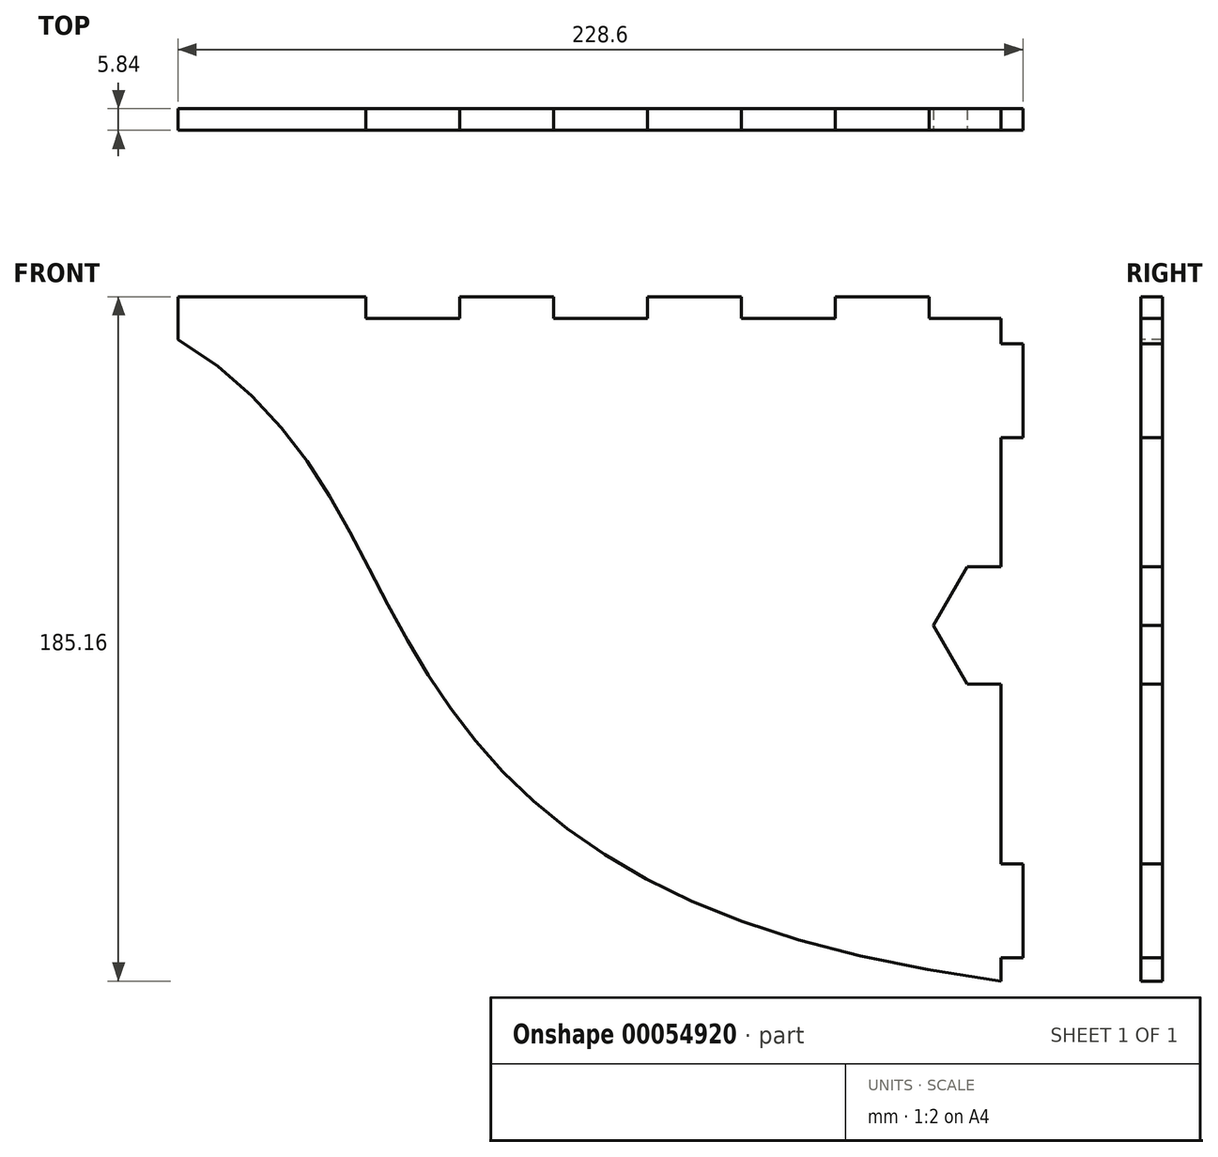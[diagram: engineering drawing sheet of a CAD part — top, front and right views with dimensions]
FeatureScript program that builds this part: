
annotation { "Feature Type Name" : "Feature", "Feature Type Description" : "" }
export const myFeature = defineFeature(function(context is Context, id is Id, definition is map)
    precondition{}
    {
        {
            var Q0;
            Q0=qCreatedBy(makeId("Front.planeOp"),FACE);
            var sketch = newSketch(context, id + "F0", { "sketchPlane" : qUnion([Q0])});
            skLineSegment(sketch, "E0.bottom", {"start": v(-113.95, 205.98) * mm, "end": v(165.45, 205.98) * mm});
            skLineSegment(sketch, "E0.top", {"start": v(-113.95, -124.22) * mm, "end": v(165.45, -124.22) * mm});
            skLineSegment(sketch, "E0.left", {"start": v(-113.95, 205.98) * mm, "end": v(-113.95, -124.22) * mm});
            skLineSegment(sketch, "E0.right", {"start": v(165.45, 205.98) * mm, "end": v(165.45, -124.22) * mm});
            skSolve(sketch);
        }
        {
            var Q0;
            Q0=makeQuery(id+"F0.imprint","IMPRINT",FACE,{"disambiguationData":[TD([[makeQuery(id+"F0.imprint","IMPRINT",EDGE,{"derivedFrom":sQuery(id+"F0.wireOp",EDGE,"E0.bottom")}),-1.0]])]});
            extrude(context, id + "F1", {"entities" : qUnion([Q0]), "depth" : 5.84 * mm});
        }
        {
            var Q0;
            Q0=makeQuery(id+"F1.opExtrude","CAP_FACE",FACE,{"disambiguationData":[OSD([sQuery(id+"F0.wireOp",EDGE,"E0.bottom"),sQuery(id+"F0.wireOp",EDGE,"E0.top"),sQuery(id+"F0.wireOp",EDGE,"E0.left"),sQuery(id+"F0.wireOp",EDGE,"E0.right")])],"isStart":false});
            var sketch = newSketch(context, id + "F2", { "sketchPlane" : qUnion([Q0])});
            skLineSegment(sketch, "E1", {"start": v(165.45, -118.38) * mm, "end": v(140.05, -118.38) * mm});
            skLineSegment(sketch, "E2", {"start": v(140.05, -118.38) * mm, "end": v(140.05, -124.22) * mm});
            skLineSegment(sketch, "E3", {"start": v(140.05, -124.22) * mm, "end": v(114.65, -124.22) * mm});
            skLineSegment(sketch, "E4", {"start": v(114.65, -124.22) * mm, "end": v(114.65, -118.38) * mm});
            skLineSegment(sketch, "E5", {"start": v(114.65, -118.38) * mm, "end": v(89.25, -118.38) * mm});
            skLineSegment(sketch, "E6", {"start": v(89.25, -118.38) * mm, "end": v(89.25, -124.22) * mm});
            skLineSegment(sketch, "E7", {"start": v(89.25, -124.22) * mm, "end": v(63.85, -124.22) * mm});
            skLineSegment(sketch, "E8", {"start": v(63.85, -124.22) * mm, "end": v(63.85, -118.38) * mm});
            skLineSegment(sketch, "E9", {"start": v(63.85, -118.38) * mm, "end": v(38.45, -118.38) * mm});
            skLineSegment(sketch, "E10", {"start": v(38.45, -118.38) * mm, "end": v(38.45, -124.22) * mm});
            skLineSegment(sketch, "E11", {"start": v(38.45, -124.22) * mm, "end": v(13.05, -124.22) * mm});
            skLineSegment(sketch, "E12", {"start": v(13.05, -124.22) * mm, "end": v(13.05, -118.38) * mm});
            skLineSegment(sketch, "E13", {"start": v(13.05, -118.38) * mm, "end": v(-12.35, -118.38) * mm});
            skLineSegment(sketch, "E14", {"start": v(-12.35, -118.38) * mm, "end": v(-12.35, -124.22) * mm});
            skLineSegment(sketch, "E15", {"start": v(-12.35, -124.22) * mm, "end": v(-37.75, -124.22) * mm});
            skLineSegment(sketch, "E16", {"start": v(-37.75, -124.22) * mm, "end": v(-37.75, -118.38) * mm});
            skLineSegment(sketch, "E17", {"start": v(-37.75, -118.38) * mm, "end": v(-113.95, -118.38) * mm});
            skLineSegment(sketch, "E18", {"start": v(-113.95, -118.38) * mm, "end": v(-113.95, -124.22) * mm});
            skLineSegment(sketch, "E19", {"start": v(-113.95, -124.22) * mm, "end": v(-37.75, -124.22) * mm});
            skLineSegment(sketch, "E20.bottom", {"start": v(165.45, -98.82) * mm, "end": v(159.6, -98.82) * mm});
            skLineSegment(sketch, "E20.top", {"start": v(165.45, -73.42) * mm, "end": v(159.6, -73.42) * mm});
            skLineSegment(sketch, "E20.left", {"start": v(165.45, -98.82) * mm, "end": v(165.45, -73.42) * mm});
            skLineSegment(sketch, "E20.right", {"start": v(159.6, -98.82) * mm, "end": v(159.6, -73.42) * mm});
            skLineSegment(sketch, "E21.bottom", {"start": v(165.45, -48.02) * mm, "end": v(159.6, -48.02) * mm});
            skLineSegment(sketch, "E21.top", {"start": v(165.45, -9.92) * mm, "end": v(159.6, -9.92) * mm});
            skLineSegment(sketch, "E21.left", {"start": v(165.45, -48.02) * mm, "end": v(165.45, -9.92) * mm});
            skLineSegment(sketch, "E21.right", {"start": v(159.6, -48.02) * mm, "end": v(159.6, -9.92) * mm});
            skLineSegment(sketch, "E22.bottom", {"start": v(-113.95, -98.82) * mm, "end": v(-108.1, -98.82) * mm});
            skLineSegment(sketch, "E22.top", {"start": v(-113.95, -73.42) * mm, "end": v(-108.1, -73.42) * mm});
            skLineSegment(sketch, "E22.left", {"start": v(-113.95, -98.82) * mm, "end": v(-113.95, -73.42) * mm});
            skLineSegment(sketch, "E22.right", {"start": v(-108.1, -98.82) * mm, "end": v(-108.1, -73.42) * mm});
            skLineSegment(sketch, "E23.bottom", {"start": v(-113.95, -48.02) * mm, "end": v(-108.1, -48.02) * mm});
            skLineSegment(sketch, "E23.top", {"start": v(-113.95, -22.62) * mm, "end": v(-108.1, -22.62) * mm});
            skLineSegment(sketch, "E23.left", {"start": v(-113.95, -48.02) * mm, "end": v(-113.95, -22.62) * mm});
            skLineSegment(sketch, "E23.right", {"start": v(-108.1, -48.02) * mm, "end": v(-108.1, -22.62) * mm});
            skLineSegment(sketch, "E24.bottom", {"start": v(-113.95, 2.78) * mm, "end": v(-108.1, 2.78) * mm});
            skLineSegment(sketch, "E24.top", {"start": v(-113.95, 28.18) * mm, "end": v(-108.1, 28.18) * mm});
            skLineSegment(sketch, "E24.left", {"start": v(-113.95, 2.78) * mm, "end": v(-113.95, 28.18) * mm});
            skLineSegment(sketch, "E24.right", {"start": v(-108.1, 2.78) * mm, "end": v(-108.1, 28.18) * mm});
            skLineSegment(sketch, "E25.bottom", {"start": v(-113.95, 104.38) * mm, "end": v(-108.1, 104.38) * mm});
            skLineSegment(sketch, "E25.top", {"start": v(-113.95, 129.78) * mm, "end": v(-108.1, 129.78) * mm});
            skLineSegment(sketch, "E25.left", {"start": v(-113.95, 104.38) * mm, "end": v(-113.95, 129.78) * mm});
            skLineSegment(sketch, "E25.right", {"start": v(-108.1, 104.38) * mm, "end": v(-108.1, 129.78) * mm});
            skLineSegment(sketch, "E26.bottom", {"start": v(-113.95, 53.58) * mm, "end": v(-108.1, 53.58) * mm});
            skLineSegment(sketch, "E26.top", {"start": v(-113.95, 78.98) * mm, "end": v(-108.1, 78.98) * mm});
            skLineSegment(sketch, "E26.left", {"start": v(-113.95, 53.58) * mm, "end": v(-113.95, 78.98) * mm});
            skLineSegment(sketch, "E26.right", {"start": v(-108.1, 53.58) * mm, "end": v(-108.1, 78.98) * mm});
            skLineSegment(sketch, "E27.bottom", {"start": v(-113.95, 155.18) * mm, "end": v(-108.1, 155.18) * mm});
            skLineSegment(sketch, "E27.top", {"start": v(-113.95, 180.58) * mm, "end": v(-108.1, 180.58) * mm});
            skLineSegment(sketch, "E27.left", {"start": v(-113.95, 155.18) * mm, "end": v(-113.95, 180.58) * mm});
            skLineSegment(sketch, "E27.right", {"start": v(-108.1, 155.18) * mm, "end": v(-108.1, 180.58) * mm});
            skSolve(sketch);
        }
        {
            var Q0;
            {var subQ0=sQuery(id+"F2.wireOp",EDGE,"E1");Q0=makeQuery(id+"F2.imprint","IMPRINT",FACE,{"disambiguationData":[TD([[makeQuery(id+"F2.imprint","IMPRINT",EDGE,{"derivedFrom":subQ0}),1.0]])]});}
            var Q1;
            {var subQ0=sQuery(id+"F2.wireOp",EDGE,"E4");Q1=makeQuery(id+"F2.imprint","IMPRINT",FACE,{"disambiguationData":[TD([[makeQuery(id+"F2.imprint","IMPRINT",EDGE,{"derivedFrom":subQ0}),1.0]])]});}
            var Q2;
            {var subQ0=sQuery(id+"F2.wireOp",EDGE,"E8");Q2=makeQuery(id+"F2.imprint","IMPRINT",FACE,{"disambiguationData":[TD([[makeQuery(id+"F2.imprint","IMPRINT",EDGE,{"derivedFrom":subQ0}),1.0]])]});}
            var Q3;
            {var subQ0=sQuery(id+"F2.wireOp",EDGE,"E12");Q3=makeQuery(id+"F2.imprint","IMPRINT",FACE,{"disambiguationData":[TD([[makeQuery(id+"F2.imprint","IMPRINT",EDGE,{"derivedFrom":subQ0}),1.0]])]});}
            var Q4;
            Q4=makeQuery(id+"F2.imprint","IMPRINT",FACE,{"disambiguationData":[TD([[makeQuery(id+"F2.imprint","IMPRINT",EDGE,{"derivedFrom":sQuery(id+"F2.wireOp",EDGE,"E16")}),1.0]])]});
            var Q5;
            Q5=makeQuery(id+"F2.imprint","IMPRINT",FACE,{"disambiguationData":[TD([[makeQuery(id+"F2.imprint","IMPRINT",EDGE,{"derivedFrom":sQuery(id+"F2.wireOp",EDGE,"E20.bottom")}),-1.0]])]});
            var Q6;
            Q6=makeQuery(id+"F2.imprint","IMPRINT",FACE,{"disambiguationData":[TD([[makeQuery(id+"F2.imprint","IMPRINT",EDGE,{"derivedFrom":sQuery(id+"F2.wireOp",EDGE,"E21.bottom")}),-1.0]])]});
            var Q7;
            Q7=makeQuery(id+"F2.imprint","IMPRINT",FACE,{"disambiguationData":[TD([[makeQuery(id+"F2.imprint","IMPRINT",EDGE,{"derivedFrom":sQuery(id+"F2.wireOp",EDGE,"E22.bottom")}),1.0]])]});
            var Q8;
            Q8=makeQuery(id+"F2.imprint","IMPRINT",FACE,{"disambiguationData":[TD([[makeQuery(id+"F2.imprint","IMPRINT",EDGE,{"derivedFrom":sQuery(id+"F2.wireOp",EDGE,"E23.bottom")}),1.0]])]});
            var Q9;
            Q9=makeQuery(id+"F2.imprint","IMPRINT",FACE,{"disambiguationData":[TD([[makeQuery(id+"F2.imprint","IMPRINT",EDGE,{"derivedFrom":sQuery(id+"F2.wireOp",EDGE,"E24.bottom")}),1.0]])]});
            var Q10;
            Q10=makeQuery(id+"F2.imprint","IMPRINT",FACE,{"disambiguationData":[TD([[makeQuery(id+"F2.imprint","IMPRINT",EDGE,{"derivedFrom":sQuery(id+"F2.wireOp",EDGE,"E26.bottom")}),1.0]])]});
            var Q11;
            Q11=makeQuery(id+"F2.imprint","IMPRINT",FACE,{"disambiguationData":[TD([[makeQuery(id+"F2.imprint","IMPRINT",EDGE,{"derivedFrom":sQuery(id+"F2.wireOp",EDGE,"E27.bottom")}),1.0]])]});
            var Q12;
            Q12=makeQuery(id+"F2.imprint","IMPRINT",FACE,{"disambiguationData":[TD([[makeQuery(id+"F2.imprint","IMPRINT",EDGE,{"derivedFrom":sQuery(id+"F2.wireOp",EDGE,"E25.bottom")}),1.0]])]});
            var Q13;
            Q13=makeQuery(id+"F1.opExtrude","CAP_FACE",FACE,{"disambiguationData":[OSD([sQuery(id+"F0.wireOp",EDGE,"E0.bottom"),sQuery(id+"F0.wireOp",EDGE,"E0.top"),sQuery(id+"F0.wireOp",EDGE,"E0.left"),sQuery(id+"F0.wireOp",EDGE,"E0.right")])],"isStart":true});
            extrude(context, id + "F3", {"entities" : qUnion([Q0, Q1, Q2, Q3, Q4, Q5, Q6, Q7, Q8, Q9, Q10, Q11, Q12]), "operationType" : NewBodyOperationType.REMOVE, "endBound" : BoundingType.UP_TO_SURFACE, "oppositeDirection" : true, "endBoundEntityFace" : qUnion([Q13]), "depth" : 25.4 * mm});
        }
        {
            var Q0;
            Q0=makeQuery(id+"F1.opExtrude","CAP_FACE",FACE,{"disambiguationData":[OSD([sQuery(id+"F0.wireOp",EDGE,"E0.bottom"),sQuery(id+"F0.wireOp",EDGE,"E0.top"),sQuery(id+"F0.wireOp",EDGE,"E0.left"),sQuery(id+"F0.wireOp",EDGE,"E0.right")])],"isStart":false});
            var sketch = newSketch(context, id + "F4", { "sketchPlane" : qUnion([Q0])});
            skPoint(sketch, "E28", {"position": v(-56.8, 205.98) * mm});
            skPoint(sketch, "E29", {"position": v(0.35, 205.98) * mm});
            skPoint(sketch, "E30", {"position": v(57.5, 205.98) * mm});
            skPoint(sketch, "E31", {"position": v(159.6, 15.48) * mm});
            skFitSpline(sketch, "E32", {"points": [v(159.6, 15.48) * mm, v(0, 86.75) * mm, v(-113.95, 205.98) * mm], "startDerivative": vector(-509.98, 75.1) * mm, "endDerivative": vector(-560.6, 77.32) * mm});
            skLineSegment(sketch, "E33", {"start": v(159.6, 15.48) * mm, "end": v(165.45, 15.48) * mm});
            skFitSpline(sketch, "E34", {"points": [v(159.6, 21.83) * mm, v(0, 112.15) * mm, v(-113.95, 212.33) * mm], "startDerivative": vector(-548.57, 72.75) * mm, "endDerivative": vector(-499.93, 79.99) * mm});
            skLineSegment(sketch, "E35", {"start": v(-113.95, 212.33) * mm, "end": v(-113.95, 205.98) * mm});
            skLineSegment(sketch, "E36", {"start": v(159.6, 21.83) * mm, "end": v(159.6, 15.48) * mm});
            skSolve(sketch);
        }
        {
            var Q0;
            Q0=makeQuery(id+"F1.opExtrude","CAP_FACE",FACE,{"disambiguationData":[OSD([sQuery(id+"F0.wireOp",EDGE,"E0.bottom"),sQuery(id+"F0.wireOp",EDGE,"E0.top"),sQuery(id+"F0.wireOp",EDGE,"E0.left"),sQuery(id+"F0.wireOp",EDGE,"E0.right")])],"isStart":false});
            var sketch = newSketch(context, id + "F5", { "sketchPlane" : qUnion([Q0])});
            skLineSegment(sketch, "E37.bottom", {"start": v(165.45, -3.57) * mm, "end": v(159.6, -3.57) * mm});
            skLineSegment(sketch, "E37.top", {"start": v(165.45, 9.13) * mm, "end": v(159.6, 9.13) * mm});
            skLineSegment(sketch, "E37.left", {"start": v(165.45, -3.57) * mm, "end": v(165.45, 9.13) * mm});
            skLineSegment(sketch, "E37.right", {"start": v(159.6, -3.57) * mm, "end": v(159.6, 9.13) * mm});
            skSolve(sketch);
        }
        {
            var Q0;
            Q0=makeQuery(id+"F5.imprint","IMPRINT",FACE,{"disambiguationData":[TD([[makeQuery(id+"F5.imprint","IMPRINT",EDGE,{"derivedFrom":sQuery(id+"F5.wireOp",EDGE,"E37.bottom")}),-1.0]])]});
            var Q1;
            Q1=makeQuery(id+"F1.opExtrude","CAP_FACE",FACE,{"disambiguationData":[OSD([sQuery(id+"F0.wireOp",EDGE,"E0.bottom"),sQuery(id+"F0.wireOp",EDGE,"E0.top"),sQuery(id+"F0.wireOp",EDGE,"E0.left"),sQuery(id+"F0.wireOp",EDGE,"E0.right")])],"isStart":true});
            extrude(context, id + "F6", {"entities" : qUnion([Q0]), "operationType" : NewBodyOperationType.REMOVE, "endBound" : BoundingType.UP_TO_SURFACE, "oppositeDirection" : true, "endBoundEntityFace" : qUnion([Q1]), "depth" : 25.4 * mm});
        }
        {
            var Q0;
            Q0=makeQuery(id+"F4.imprint","IMPRINT",FACE,{"disambiguationData":[TD([[makeQuery(id+"F4.imprint","IMPRINT",EDGE,{"derivedFrom":sQuery(id+"F4.wireOp",EDGE,"E32")}),1.0]])]});
            var Q1;
            {var subQ0=sQuery(id+"F4.wireOp",EDGE,"E32");Q1=makeQuery(id+"F4.imprint","IMPRINT",FACE,{"disambiguationData":[TD([[makeQuery(id+"F4.imprint","IMPRINT",EDGE,{"derivedFrom":subQ0}),-1.0]])]});}
            var Q2;
            Q2=makeQuery(id+"F1.opExtrude","CAP_FACE",FACE,{"disambiguationData":[OSD([sQuery(id+"F0.wireOp",EDGE,"E0.bottom"),sQuery(id+"F0.wireOp",EDGE,"E0.top"),sQuery(id+"F0.wireOp",EDGE,"E0.left"),sQuery(id+"F0.wireOp",EDGE,"E0.right")])],"isStart":true});
            extrude(context, id + "F7", {"entities" : qUnion([Q0, Q1]), "operationType" : NewBodyOperationType.REMOVE, "endBound" : BoundingType.UP_TO_SURFACE, "oppositeDirection" : true, "endBoundEntityFace" : qUnion([Q2]), "depth" : 25.4 * mm});
        }
        {
            var Q0;
            Q0=makeQuery(id+"F1.opExtrude","CAP_FACE",FACE,{"disambiguationData":[OSD([sQuery(id+"F0.wireOp",EDGE,"E0.bottom"),sQuery(id+"F0.wireOp",EDGE,"E0.top"),sQuery(id+"F0.wireOp",EDGE,"E0.left"),sQuery(id+"F0.wireOp",EDGE,"E0.right")])],"isStart":false});
            var sketch = newSketch(context, id + "F8", { "sketchPlane" : qUnion([Q0])});
            skLineSegment(sketch, "E38.bottom", {"start": v(165.45, 28.18) * mm, "end": v(159.6, 28.18) * mm});
            skLineSegment(sketch, "E38.top", {"start": v(165.45, 53.58) * mm, "end": v(159.6, 53.58) * mm});
            skLineSegment(sketch, "E38.left", {"start": v(165.45, 28.18) * mm, "end": v(165.45, 53.58) * mm});
            skLineSegment(sketch, "E38.right", {"start": v(159.6, 28.18) * mm, "end": v(159.6, 53.58) * mm});
            skLineSegment(sketch, "E39.bottom", {"start": v(165.45, 168.9) * mm, "end": v(159.6, 168.9) * mm});
            skLineSegment(sketch, "E39.top", {"start": v(165.45, 194.3) * mm, "end": v(159.6, 194.3) * mm});
            skLineSegment(sketch, "E39.left", {"start": v(165.45, 168.9) * mm, "end": v(165.45, 194.3) * mm});
            skLineSegment(sketch, "E39.right", {"start": v(159.6, 168.9) * mm, "end": v(159.6, 194.3) * mm});
            skLineSegment(sketch, "E40", {"start": v(159.6, 194.3) * mm, "end": v(159.6, 205.98) * mm});
            skLineSegment(sketch, "E41", {"start": v(159.6, 168.9) * mm, "end": v(159.6, 53.58) * mm});
            skLineSegment(sketch, "E42", {"start": v(159.6, 28.18) * mm, "end": v(159.6, 21.83) * mm});
            skCircle(sketch, "E43", {"center": v(159.6, 118.1) * mm, "radius": 15.88 * mm});
            skCircle(sketch, "E44.cCircle", {"center": v(159.6, 118.1) * mm, "radius": 15.87 * mm, "construction": true});
            skLineSegment(sketch, "E44.0", {"start": v(150.44, 133.97) * mm, "end": v(168.77, 133.97) * mm});
            skLineSegment(sketch, "E44.1", {"start": v(168.77, 133.97) * mm, "end": v(177.94, 118.1) * mm});
            skLineSegment(sketch, "E44.2", {"start": v(177.94, 118.1) * mm, "end": v(168.77, 102.22) * mm});
            skLineSegment(sketch, "E44.3", {"start": v(168.77, 102.22) * mm, "end": v(150.44, 102.22) * mm});
            skLineSegment(sketch, "E44.4", {"start": v(150.44, 102.22) * mm, "end": v(141.28, 118.1) * mm});
            skLineSegment(sketch, "E44.5", {"start": v(141.28, 118.1) * mm, "end": v(150.44, 133.97) * mm});
            skPoint(sketch, "E44.0.midPoint", {"position": v(159.6, 133.97) * mm});
            skSolve(sketch);
        }
        {
            var Q0;
            {var subQ0=sQuery(id+"F8.wireOp",EDGE,"E38.top");Q0=makeQuery(id+"F8.imprint","IMPRINT",FACE,{"disambiguationData":[TD([[makeQuery(id+"F8.imprint","IMPRINT",EDGE,{"derivedFrom":subQ0}),-1.0]])]});}
            var Q1;
            {var subQ1=sQuery(id+"F8.wireOp",EDGE,"E38.bottom");Q1=makeQuery(id+"F8.imprint","IMPRINT",FACE,{"disambiguationData":[TD([[makeQuery(id+"F8.imprint","IMPRINT",EDGE,{"derivedFrom":subQ1}),1.0]])]});}
            var Q2;
            {var subQ0=sQuery(id+"F8.wireOp",EDGE,"E38.top");Q2=makeQuery(id+"F8.imprint","IMPRINT",FACE,{"disambiguationData":[TD([[makeQuery(id+"F8.imprint","IMPRINT",EDGE,{"derivedFrom":subQ0}),-1.0]])]});}
            var Q3;
            {var subQ0=sQuery(id+"F8.wireOp",EDGE,"E39.top");Q3=makeQuery(id+"F8.imprint","IMPRINT",FACE,{"disambiguationData":[TD([[makeQuery(id+"F8.imprint","IMPRINT",EDGE,{"derivedFrom":subQ0}),-1.0]])]});}
            var Q4;
            {var subQ0=sQuery(id+"F8.wireOp",EDGE,"E39.bottom");Q4=makeQuery(id+"F8.imprint","IMPRINT",FACE,{"disambiguationData":[TD([[makeQuery(id+"F8.imprint","IMPRINT",EDGE,{"derivedFrom":subQ0}),1.0]])]});}
            var Q5;
            {var subQ0=sQuery(id+"F8.wireOp",EDGE,"E43");var subQ4=makeQuery(id+"F8.imprint","INTERSECT",VERTEX,{"derivedFrom":[subQ0,sQuery(id+"F8.wireOp",EDGE,"E44.5")]});Q5=makeQuery(id+"F8.imprint","IMPRINT",FACE,{"disambiguationData":[TD([[makeQuery(id+"F8.imprint","IMPRINT",EDGE,{"disambiguationData":[TD([[subQ4,-1.0]])],"derivedFrom":subQ0}),1.0]])]});}
            var Q6;
            {var subQ0=sQuery(id+"F8.wireOp",EDGE,"E44.5");var subQ3=sQuery(id+"F8.wireOp",EDGE,"E44.0");var subQ5=makeQuery(id+"F8.imprint","INTERSECT",VERTEX,{"derivedFrom":[subQ3,subQ0]});Q6=makeQuery(id+"F8.imprint","IMPRINT",FACE,{"disambiguationData":[TD([[makeQuery(id+"F8.imprint","IMPRINT",EDGE,{"disambiguationData":[TD([[subQ5,1.0]])],"derivedFrom":subQ0}),-1.0]])]});}
            var Q7;
            {var subQ0=sQuery(id+"F8.wireOp",EDGE,"E44.5");var subQ1=sQuery(id+"F8.wireOp",EDGE,"E43");var subQ2=makeQuery(id+"F8.imprint","INTERSECT",VERTEX,{"derivedFrom":[subQ1,subQ0]});Q7=makeQuery(id+"F8.imprint","IMPRINT",FACE,{"disambiguationData":[TD([[makeQuery(id+"F8.imprint","IMPRINT",EDGE,{"disambiguationData":[TD([[subQ2,-1.0]])],"derivedFrom":subQ1}),-1.0]])]});}
            var Q8;
            {var subQ0=sQuery(id+"F8.wireOp",EDGE,"E44.4");var subQ3=sQuery(id+"F8.wireOp",EDGE,"E44.3");var subQ5=makeQuery(id+"F8.imprint","INTERSECT",VERTEX,{"derivedFrom":[subQ3,subQ0]});Q8=makeQuery(id+"F8.imprint","IMPRINT",FACE,{"disambiguationData":[TD([[makeQuery(id+"F8.imprint","IMPRINT",EDGE,{"disambiguationData":[TD([[subQ5,-1.0]])],"derivedFrom":subQ0}),-1.0]])]});}
            var Q9;
            {var subQ0=sQuery(id+"F8.wireOp",EDGE,"E44.3");var subQ1=sQuery(id+"F8.wireOp",EDGE,"E43");var subQ2=makeQuery(id+"F8.imprint","INTERSECT",VERTEX,{"derivedFrom":[sQuery(id+"F8.wireOp",EDGE,"E41"),subQ1,subQ0]});Q9=makeQuery(id+"F8.imprint","IMPRINT",FACE,{"disambiguationData":[TD([[makeQuery(id+"F8.imprint","IMPRINT",EDGE,{"disambiguationData":[TD([[subQ2,-1.0]])],"derivedFrom":subQ1}),-1.0]])]});}
            var Q10;
            {var subQ0=sQuery(id+"F8.wireOp",EDGE,"E43");var subQ1=sQuery(id+"F8.wireOp",EDGE,"E41");var subQ2=makeQuery(id+"F8.imprint","INTERSECT",VERTEX,{"derivedFrom":[subQ1,subQ0,sQuery(id+"F8.wireOp",EDGE,"E44.0")]});Q10=makeQuery(id+"F8.imprint","IMPRINT",FACE,{"disambiguationData":[TD([[makeQuery(id+"F8.imprint","IMPRINT",EDGE,{"disambiguationData":[TD([[subQ2,-1.0]])],"derivedFrom":subQ1}),1.0]])]});}
            var Q11;
            {var subQ0=sQuery(id+"F8.wireOp",EDGE,"E44.0");var subQ1=sQuery(id+"F8.wireOp",EDGE,"E43");var subQ2=makeQuery(id+"F8.imprint","INTERSECT",VERTEX,{"derivedFrom":[sQuery(id+"F8.wireOp",EDGE,"E41"),subQ1,subQ0]});Q11=makeQuery(id+"F8.imprint","IMPRINT",FACE,{"disambiguationData":[TD([[makeQuery(id+"F8.imprint","IMPRINT",EDGE,{"disambiguationData":[TD([[subQ2,1.0]])],"derivedFrom":subQ1}),-1.0]])]});}
            var Q12;
            Q12=makeQuery(id+"F1.opExtrude","CAP_FACE",FACE,{"disambiguationData":[OSD([sQuery(id+"F0.wireOp",EDGE,"E0.bottom"),sQuery(id+"F0.wireOp",EDGE,"E0.top"),sQuery(id+"F0.wireOp",EDGE,"E0.left"),sQuery(id+"F0.wireOp",EDGE,"E0.right")])],"isStart":true});
            extrude(context, id + "F9", {"entities" : qUnion([Q0, Q1, Q2, Q3, Q4, Q5, Q6, Q7, Q8, Q9, Q10, Q11]), "operationType" : NewBodyOperationType.REMOVE, "endBound" : BoundingType.UP_TO_SURFACE, "oppositeDirection" : true, "endBoundEntityFace" : qUnion([Q12]), "depth" : 25.4 * mm});
        }
        {
            var Q0;
            Q0=makeQuery(id+"F1.opExtrude","CAP_FACE",FACE,{"disambiguationData":[OSD([sQuery(id+"F0.wireOp",EDGE,"E0.bottom"),sQuery(id+"F0.wireOp",EDGE,"E0.top"),sQuery(id+"F0.wireOp",EDGE,"E0.left"),sQuery(id+"F0.wireOp",EDGE,"E0.right")])],"isStart":false});
            var sketch = newSketch(context, id + "F10", { "sketchPlane" : qUnion([Q0])});
            skLineSegment(sketch, "E45.bottom", {"start": v(159.6, 205.98) * mm, "end": v(-87.11, 205.98) * mm});
            skLineSegment(sketch, "E45.top", {"start": v(159.6, 207) * mm, "end": v(-87.11, 207) * mm});
            skLineSegment(sketch, "E45.left", {"start": v(159.6, 205.98) * mm, "end": v(159.6, 207) * mm});
            skLineSegment(sketch, "E45.right", {"start": v(-87.11, 205.98) * mm, "end": v(-87.11, 207) * mm});
            skSolve(sketch);
        }
        {
            var Q0;
            Q0=makeQuery(id+"F10.imprint","IMPRINT",FACE,{"disambiguationData":[TD([[makeQuery(id+"F10.imprint","IMPRINT",EDGE,{"derivedFrom":sQuery(id+"F10.wireOp",EDGE,"E45.bottom")}),1.0]])]});
            var Q1;
            Q1=makeQuery(id+"F1.opExtrude","CAP_FACE",FACE,{"disambiguationData":[OSD([sQuery(id+"F0.wireOp",EDGE,"E0.bottom"),sQuery(id+"F0.wireOp",EDGE,"E0.top"),sQuery(id+"F0.wireOp",EDGE,"E0.left"),sQuery(id+"F0.wireOp",EDGE,"E0.right")])],"isStart":true});
            extrude(context, id + "F11", {"entities" : qUnion([Q0]), "operationType" : NewBodyOperationType.ADD, "endBound" : BoundingType.UP_TO_SURFACE, "oppositeDirection" : true, "endBoundEntityFace" : qUnion([Q1]), "depth" : 25.4 * mm});
        }
        {
            var Q0;
            Q0=makeQuery(id+"F11.boolean.opBoolean","MERGE",FACE,{"derivedFrom":[makeQuery(id+"F1.opExtrude","CAP_FACE",FACE,{"disambiguationData":[OSD([sQuery(id+"F0.wireOp",EDGE,"E0.bottom"),sQuery(id+"F0.wireOp",EDGE,"E0.top"),sQuery(id+"F0.wireOp",EDGE,"E0.left"),sQuery(id+"F0.wireOp",EDGE,"E0.right")])],"isStart":false}),makeQuery(id+"F11.opExtrude","CAP_FACE",FACE,{"disambiguationData":[OSD([sQuery(id+"F10.wireOp",EDGE,"E45.bottom"),sQuery(id+"F10.wireOp",EDGE,"E45.top"),sQuery(id+"F10.wireOp",EDGE,"E45.left"),sQuery(id+"F10.wireOp",EDGE,"E45.right")])],"isStart":true})]});
            var sketch = newSketch(context, id + "F12", { "sketchPlane" : qUnion([Q0])});
            skLineSegment(sketch, "E46.bottom", {"start": v(159.6, 201.15) * mm, "end": v(140.05, 201.15) * mm});
            skLineSegment(sketch, "E46.top", {"start": v(159.6, 207) * mm, "end": v(140.05, 207) * mm});
            skLineSegment(sketch, "E46.left", {"start": v(159.6, 201.15) * mm, "end": v(159.6, 207) * mm});
            skLineSegment(sketch, "E46.right", {"start": v(140.05, 201.15) * mm, "end": v(140.05, 207) * mm});
            skLineSegment(sketch, "E47.bottom", {"start": v(114.65, 207) * mm, "end": v(89.25, 207) * mm});
            skLineSegment(sketch, "E47.top", {"start": v(114.65, 201.15) * mm, "end": v(89.25, 201.15) * mm});
            skLineSegment(sketch, "E47.left", {"start": v(114.65, 207) * mm, "end": v(114.65, 201.15) * mm});
            skLineSegment(sketch, "E47.right", {"start": v(89.25, 207) * mm, "end": v(89.25, 201.15) * mm});
            skLineSegment(sketch, "E48.bottom", {"start": v(63.85, 207) * mm, "end": v(38.45, 207) * mm});
            skLineSegment(sketch, "E48.top", {"start": v(63.85, 201.15) * mm, "end": v(38.45, 201.15) * mm});
            skLineSegment(sketch, "E48.left", {"start": v(63.85, 207) * mm, "end": v(63.85, 201.15) * mm});
            skLineSegment(sketch, "E48.right", {"start": v(38.45, 207) * mm, "end": v(38.45, 201.15) * mm});
            skPoint(sketch, "E49", {"position": v(-36.31, 172.98) * mm});
            skFitSpline(sketch, "E50", {"points": [v(-36.31, 172.98) * mm, v(-61.71, 192.03) * mm, v(-64.89, 207) * mm], "startDerivative": vector(-51.63, 38.72) * mm, "endDerivative": vector(-4.65, 81.64) * mm});
            skLineSegment(sketch, "E51.bottom", {"start": v(13.05, 207) * mm, "end": v(-12.35, 207) * mm});
            skLineSegment(sketch, "E51.top", {"start": v(13.05, 201.15) * mm, "end": v(-12.35, 201.15) * mm});
            skLineSegment(sketch, "E51.left", {"start": v(13.05, 207) * mm, "end": v(13.05, 201.15) * mm});
            skLineSegment(sketch, "E51.right", {"start": v(-12.35, 207) * mm, "end": v(-12.35, 201.15) * mm});
            skLineSegment(sketch, "E52", {"start": v(-63.15, 207) * mm, "end": v(-63.15, 193.64) * mm});
            skSolve(sketch);
        }
        {
            var Q0;
            Q0=makeQuery(id+"F12.imprint","IMPRINT",FACE,{"disambiguationData":[TD([[makeQuery(id+"F12.imprint","IMPRINT",EDGE,{"derivedFrom":sQuery(id+"F12.wireOp",EDGE,"E48.bottom")}),1.0]])]});
            var Q1;
            Q1=makeQuery(id+"F12.imprint","IMPRINT",FACE,{"disambiguationData":[TD([[makeQuery(id+"F12.imprint","IMPRINT",EDGE,{"derivedFrom":sQuery(id+"F12.wireOp",EDGE,"E47.bottom")}),1.0]])]});
            var Q2;
            Q2=makeQuery(id+"F12.imprint","IMPRINT",FACE,{"disambiguationData":[TD([[makeQuery(id+"F12.imprint","IMPRINT",EDGE,{"derivedFrom":sQuery(id+"F12.wireOp",EDGE,"E46.bottom")}),-1.0]])]});
            var Q3;
            {var subQ5=makeQuery(id+"F11.opExtrude","CAP_EDGE",EDGE,{"disambiguationData":[OSD([sQuery(id+"F10.wireOp",EDGE,"E45.right")])],"isStart":true});Q3=makeQuery(id+"F12.imprint","IMPRINT",FACE,{"disambiguationData":[TD([[makeQuery(id+"F12.imprint","IMPRINT",EDGE,{"derivedFrom":subQ5}),-1.0]])]});}
            var Q4;
            Q4=makeQuery(id+"F12.imprint","IMPRINT",FACE,{"disambiguationData":[TD([[makeQuery(id+"F12.imprint","IMPRINT",EDGE,{"derivedFrom":sQuery(id+"F12.wireOp",EDGE,"E51.bottom")}),1.0]])]});
            var Q5;
            {var subQ0=sQuery(id+"F12.wireOp",EDGE,"E50");var subQ1=makeQuery(id+"F11.opExtrude","CAP_EDGE",EDGE,{"disambiguationData":[OSD([sQuery(id+"F10.wireOp",EDGE,"E45.top")])],"isStart":true});var subQ2=makeQuery(id+"F12.imprint","INTERSECT",VERTEX,{"derivedFrom":[subQ1,subQ0]});Q5=makeQuery(id+"F12.imprint","IMPRINT",FACE,{"disambiguationData":[TD([[makeQuery(id+"F12.imprint","IMPRINT",EDGE,{"disambiguationData":[TD([[subQ2,1.0]])],"derivedFrom":subQ0}),-1.0]])]});}
            var Q6;
            Q6=makeQuery(id+"F11.boolean.opBoolean","MERGE",FACE,{"derivedFrom":[makeQuery(id+"F1.opExtrude","CAP_FACE",FACE,{"disambiguationData":[OSD([sQuery(id+"F0.wireOp",EDGE,"E0.bottom"),sQuery(id+"F0.wireOp",EDGE,"E0.top"),sQuery(id+"F0.wireOp",EDGE,"E0.left"),sQuery(id+"F0.wireOp",EDGE,"E0.right")])],"isStart":true}),makeQuery(id+"F11.opExtrude","CAP_FACE",FACE,{"disambiguationData":[OSD([sQuery(id+"F10.wireOp",EDGE,"E45.bottom"),sQuery(id+"F10.wireOp",EDGE,"E45.top"),sQuery(id+"F10.wireOp",EDGE,"E45.left"),sQuery(id+"F10.wireOp",EDGE,"E45.right")])],"isStart":false})]});
            extrude(context, id + "F13", {"entities" : qUnion([Q0, Q1, Q2, Q3, Q4, Q5]), "operationType" : NewBodyOperationType.REMOVE, "endBound" : BoundingType.UP_TO_SURFACE, "oppositeDirection" : true, "endBoundEntityFace" : qUnion([Q6]), "depth" : 25.4 * mm});
        }
    });
